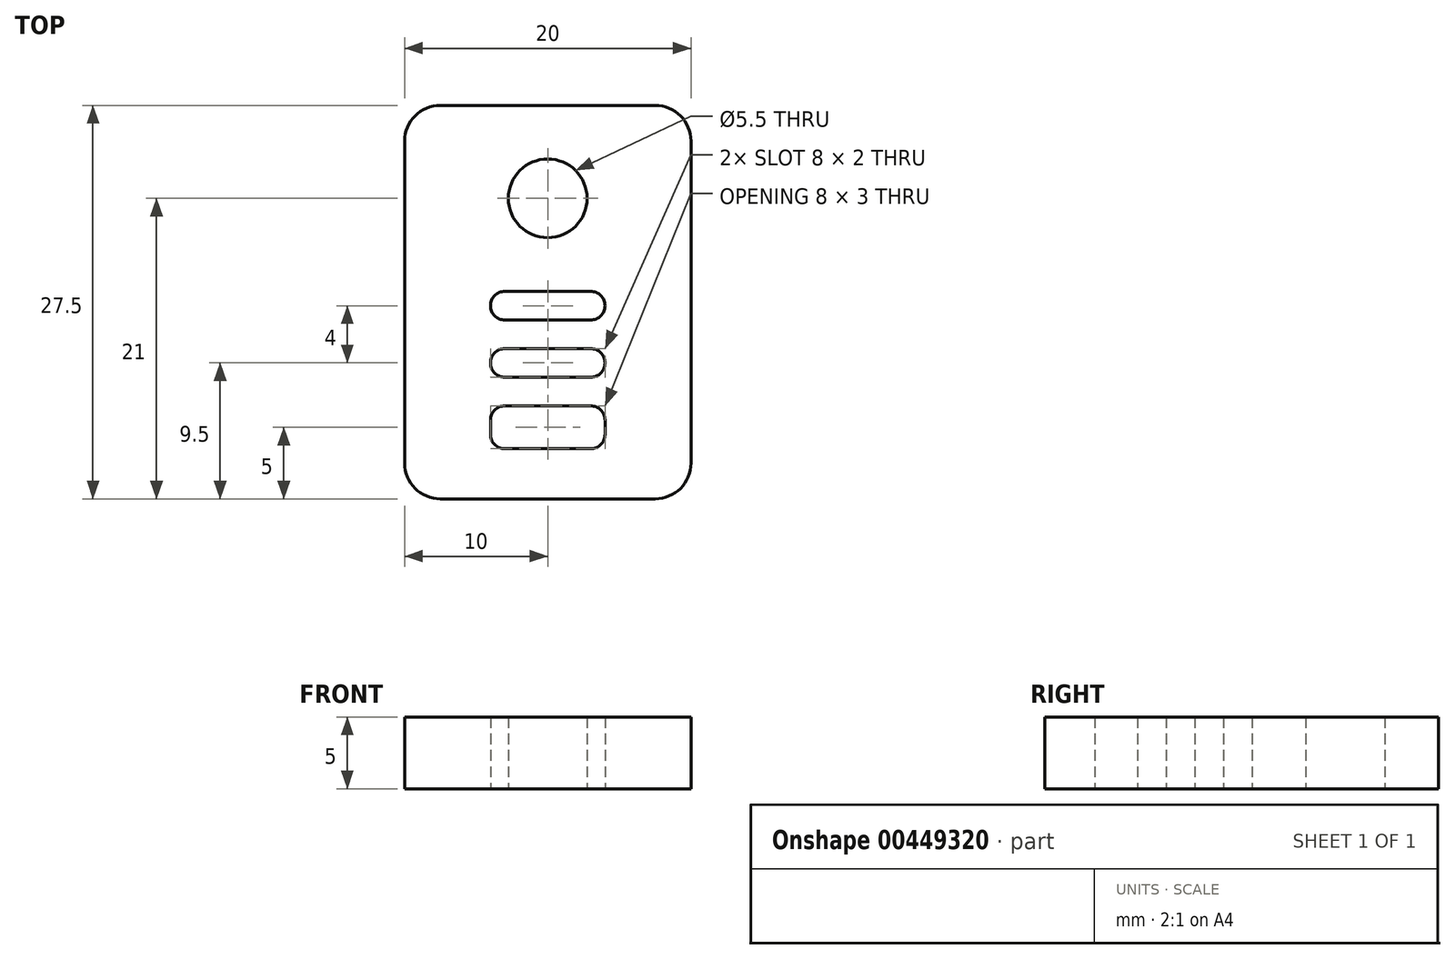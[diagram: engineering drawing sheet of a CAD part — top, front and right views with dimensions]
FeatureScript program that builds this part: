
annotation { "Feature Type Name" : "Feature", "Feature Type Description" : "" }
export const myFeature = defineFeature(function(context is Context, id is Id, definition is map)
    precondition{}
    {
        {
            var Q0;
            Q0=qCreatedBy(makeId("Top.planeOp"),FACE);
            var sketch = newSketch(context, id + "F0", { "sketchPlane" : qUnion([Q0])});
            skLineSegment(sketch, "E0.bottom", {"start": v(-7.5, 6.5) * mm, "end": v(7.5, 6.5) * mm});
            skLineSegment(sketch, "E0.top", {"start": v(-7.5, -21) * mm, "end": v(7.5, -21) * mm});
            skLineSegment(sketch, "E0.left", {"start": v(-10, 4) * mm, "end": v(-10, -18.5) * mm});
            skLineSegment(sketch, "E0.right", {"start": v(10, 4) * mm, "end": v(10, -18.5) * mm});
            skCircle(sketch, "E1", {"center": v(0, 0) * mm, "radius": 2.75 * mm});
            skLineSegment(sketch, "E2.bottom", {"start": v(-3, -14.5) * mm, "end": v(3, -14.5) * mm});
            skLineSegment(sketch, "E2.top", {"start": v(-3, -17.5) * mm, "end": v(3, -17.5) * mm});
            skLineSegment(sketch, "E2.left", {"start": v(-4, -15.5) * mm, "end": v(-4, -16.5) * mm});
            skLineSegment(sketch, "E2.right", {"start": v(4, -15.5) * mm, "end": v(4, -16.5) * mm});
            skLineSegment(sketch, "E3.bottom", {"start": v(-3, -12.5) * mm, "end": v(3, -12.5) * mm});
            skLineSegment(sketch, "E3.top", {"start": v(-3, -10.5) * mm, "end": v(3, -10.5) * mm});
            skLineSegment(sketch, "E3.left", {"start": v(-4, -11.5) * mm, "end": v(-4, -11.5) * mm});
            skLineSegment(sketch, "E3.right", {"start": v(4, -11.5) * mm, "end": v(4, -11.5) * mm});
            skLineSegment(sketch, "E4.bottom", {"start": v(3, -8.5) * mm, "end": v(-3, -8.5) * mm});
            skLineSegment(sketch, "E4.top", {"start": v(3, -6.5) * mm, "end": v(-3, -6.5) * mm});
            skLineSegment(sketch, "E4.left", {"start": v(4, -7.5) * mm, "end": v(4, -7.5) * mm});
            skLineSegment(sketch, "E4.right", {"start": v(-4, -7.5) * mm, "end": v(-4, -7.5) * mm});
            skPoint(sketch, "E5.visualSharp", {"position": v(-10, 6.5) * mm});
            skArc(sketch, "E5.filletArc", {"start": v(-7.5, 6.5) * mm, "mid": v(-9.27, 5.77) * mm, "end": v(-10, 4) * mm});
            skPoint(sketch, "E6.visualSharp", {"position": v(10, 6.5) * mm});
            skArc(sketch, "E6.filletArc", {"start": v(10, 4) * mm, "mid": v(9.27, 5.77) * mm, "end": v(7.5, 6.5) * mm});
            skPoint(sketch, "E7.visualSharp", {"position": v(10, -21) * mm});
            skArc(sketch, "E7.filletArc", {"start": v(7.5, -21) * mm, "mid": v(9.27, -20.27) * mm, "end": v(10, -18.5) * mm});
            skPoint(sketch, "E8.visualSharp", {"position": v(-10, -21) * mm});
            skArc(sketch, "E8.filletArc", {"start": v(-10, -18.5) * mm, "mid": v(-9.27, -20.27) * mm, "end": v(-7.5, -21) * mm});
            skPoint(sketch, "E9.visualSharp", {"position": v(-4, -14.5) * mm});
            skArc(sketch, "E9.filletArc", {"start": v(-3, -14.5) * mm, "mid": v(-3.7, -14.8) * mm, "end": v(-4, -15.5) * mm});
            skPoint(sketch, "E10.visualSharp", {"position": v(-4, -17.5) * mm});
            skArc(sketch, "E10.filletArc", {"start": v(-4, -16.5) * mm, "mid": v(-3.7, -17.2) * mm, "end": v(-3, -17.5) * mm});
            skPoint(sketch, "E11.visualSharp", {"position": v(4, -17.5) * mm});
            skArc(sketch, "E11.filletArc", {"start": v(3, -17.5) * mm, "mid": v(3.7, -17.2) * mm, "end": v(4, -16.5) * mm});
            skPoint(sketch, "E12.visualSharp", {"position": v(4, -14.5) * mm});
            skArc(sketch, "E12.filletArc", {"start": v(4, -15.5) * mm, "mid": v(3.7, -14.8) * mm, "end": v(3, -14.5) * mm});
            skPoint(sketch, "E13.visualSharp", {"position": v(4, -12.5) * mm});
            skArc(sketch, "E13.filletArc", {"start": v(3, -12.5) * mm, "mid": v(3.7, -12.2) * mm, "end": v(4, -11.5) * mm});
            skPoint(sketch, "E14.visualSharp", {"position": v(4, -10.5) * mm});
            skArc(sketch, "E14.filletArc", {"start": v(4, -11.5) * mm, "mid": v(3.7, -10.8) * mm, "end": v(3, -10.5) * mm});
            skPoint(sketch, "E15.visualSharp", {"position": v(4, -8.5) * mm});
            skArc(sketch, "E15.filletArc", {"start": v(3, -8.5) * mm, "mid": v(3.7, -8.2) * mm, "end": v(4, -7.5) * mm});
            skPoint(sketch, "E16.visualSharp", {"position": v(4, -6.5) * mm});
            skArc(sketch, "E16.filletArc", {"start": v(4, -7.5) * mm, "mid": v(3.7, -6.8) * mm, "end": v(3, -6.5) * mm});
            skPoint(sketch, "E17.visualSharp", {"position": v(-4, -6.5) * mm});
            skArc(sketch, "E17.filletArc", {"start": v(-3, -6.5) * mm, "mid": v(-3.7, -6.8) * mm, "end": v(-4, -7.5) * mm});
            skPoint(sketch, "E18.visualSharp", {"position": v(-4, -8.5) * mm});
            skArc(sketch, "E18.filletArc", {"start": v(-4, -7.5) * mm, "mid": v(-3.7, -8.2) * mm, "end": v(-3, -8.5) * mm});
            skPoint(sketch, "E19.visualSharp", {"position": v(-4, -10.5) * mm});
            skArc(sketch, "E19.filletArc", {"start": v(-3, -10.5) * mm, "mid": v(-3.7, -10.8) * mm, "end": v(-4, -11.5) * mm});
            skPoint(sketch, "E20.visualSharp", {"position": v(-4, -12.5) * mm});
            skArc(sketch, "E20.filletArc", {"start": v(-4, -11.5) * mm, "mid": v(-3.7, -12.2) * mm, "end": v(-3, -12.5) * mm});
            skSolve(sketch);
        }
        {
            var Q0;
            Q0=qSketchRegion(id+"F0",true);
            extrude(context, id + "F1", {"entities" : qUnion([Q0]), "depth" : 5 * mm});
        }
    });
